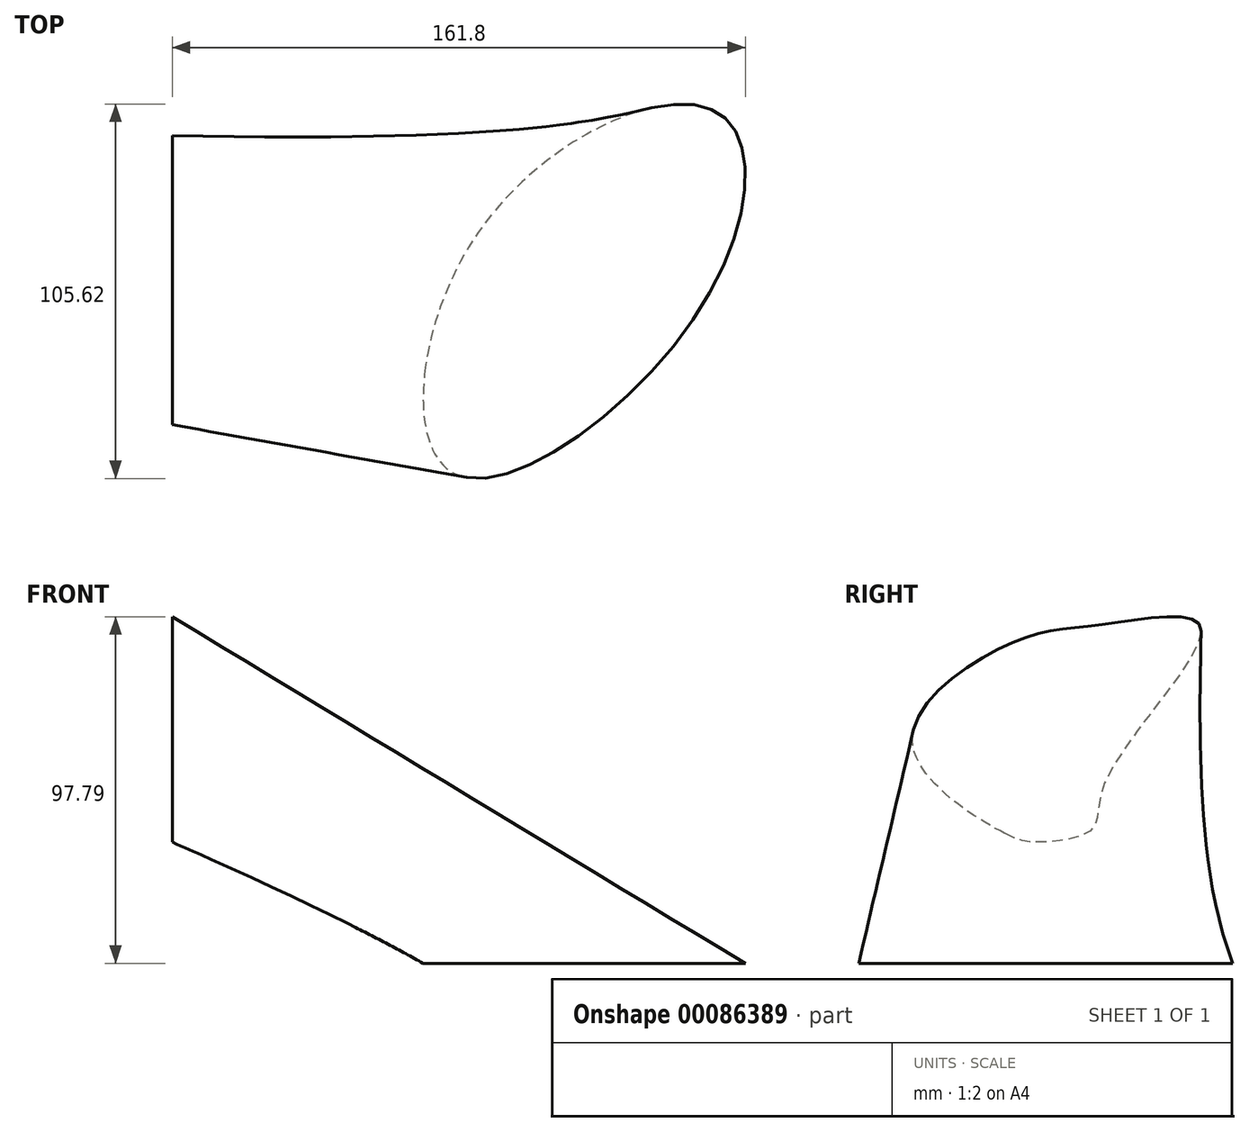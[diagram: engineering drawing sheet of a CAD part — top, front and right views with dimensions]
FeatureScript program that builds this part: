
annotation { "Feature Type Name" : "Feature", "Feature Type Description" : "" }
export const myFeature = defineFeature(function(context is Context, id is Id, definition is map)
    precondition{}
    {
        {
            var Q0;
            Q0=qCreatedBy(makeId("Right.planeOp"),FACE);
            var sketch = newSketch(context, id + "F0", { "sketchPlane" : qUnion([Q0])});
            skFitSpline(sketch, "E0", {"points": [v(-28.57, 36.71) * mm, v(-54.56, 62.38) * mm, v(-26.67, 90.32) * mm, v(0, 95.72) * mm, v(26.84, 94.78) * mm, v(0, 51.53) * mm, v(-3.98, 37.67) * mm, v(-18.7, 34.2) * mm, v(-28.57, 36.71) * mm]});
            skSolve(sketch);
        }
        {
            var Q0;
            Q0=qCreatedBy(makeId("Top.planeOp"),FACE);
            var sketch = newSketch(context, id + "F1", { "sketchPlane" : qUnion([Q0])});
            skFitSpline(sketch, "E1", {"points": [v(153.82, 33.6) * mm, v(86.6, 0) * mm, v(79.43, -68.22) * mm, v(149.29, -21.5) * mm, v(153.82, 33.6) * mm]});
            skSolve(sketch);
        }
        {
            var Q0;
            Q0=makeQuery(id+"F0.imprint","IMPRINT",FACE,{"disambiguationData":[TD([[makeQuery(id+"F0.imprint","IMPRINT",EDGE,{"derivedFrom":sQuery(id+"F0.wireOp",EDGE,"E0")}),-1.0]])]});
            var Q1;
            Q1=makeQuery(id+"F1.imprint","IMPRINT",FACE,{"disambiguationData":[TD([[makeQuery(id+"F1.imprint","IMPRINT",EDGE,{"derivedFrom":sQuery(id+"F1.wireOp",EDGE,"E1")}),1.0]])]});
            loft(context, id + "F2", {"sheetProfilesArray" : [{ "sheetProfileEntities" : qUnion([Q0]) }, { "sheetProfileEntities" : qUnion([Q1]) }]});
        }
    });
